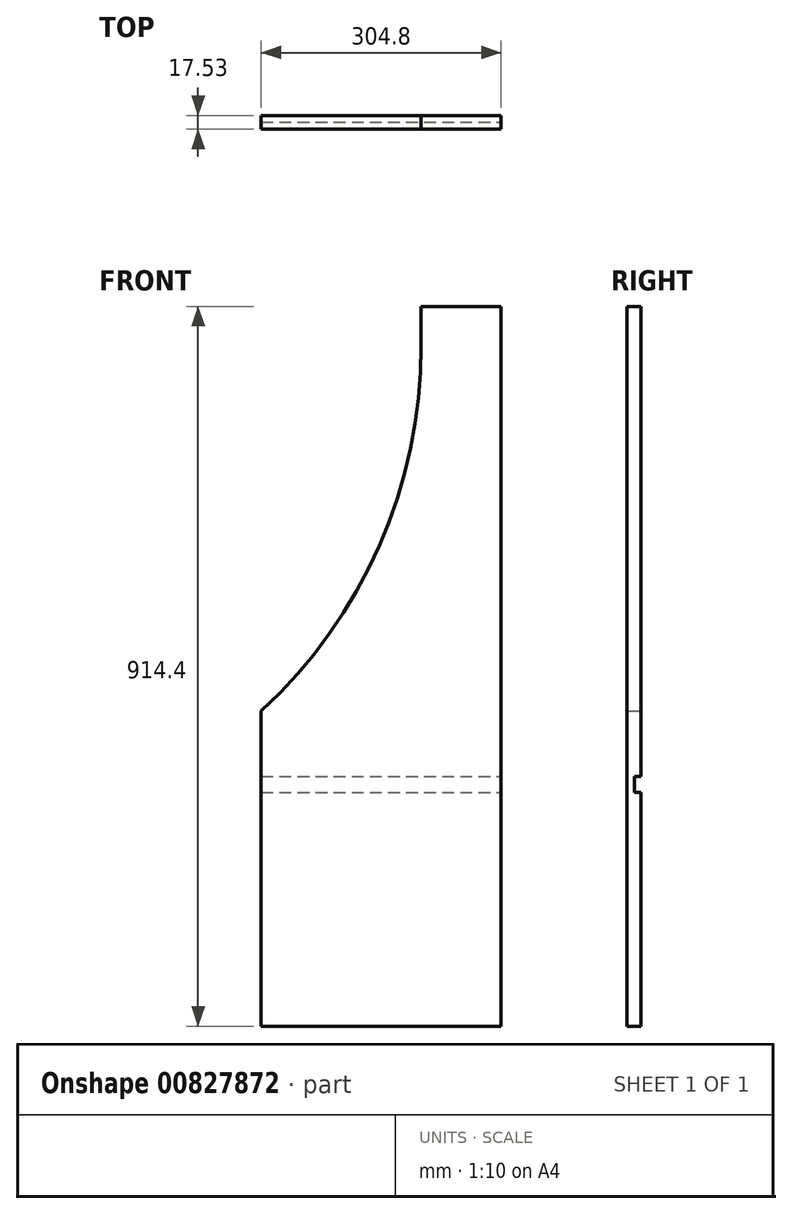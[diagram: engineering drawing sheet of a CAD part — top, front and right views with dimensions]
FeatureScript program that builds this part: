
annotation { "Feature Type Name" : "Feature", "Feature Type Description" : "" }
export const myFeature = defineFeature(function(context is Context, id is Id, definition is map)
    precondition{}
    {
        {
            var Q0;
            Q0=qCreatedBy(makeId("Front.planeOp"),FACE);
            var sketch = newSketch(context, id + "F0", { "sketchPlane" : qUnion([Q0])});
            skLineSegment(sketch, "E0", {"start": v(-178.85, -637.23) * mm, "end": v(125.95, -637.23) * mm});
            skLineSegment(sketch, "E1", {"start": v(125.95, -637.23) * mm, "end": v(125.95, 277.17) * mm});
            skLineSegment(sketch, "E2", {"start": v(125.95, 277.17) * mm, "end": v(24.35, 277.17) * mm});
            skLineSegment(sketch, "E3", {"start": v(24.35, 277.17) * mm, "end": v(24.35, 226.37) * mm});
            skLineSegment(sketch, "E4", {"start": v(-178.85, -637.23) * mm, "end": v(-178.85, -319.73) * mm});
            skArc(sketch, "E5", {"start": v(-178.85, -236.92) * mm, "mid": v(-28.68, -26.58) * mm, "end": v(24.35, 226.37) * mm});
            skLineSegment(sketch, "E6", {"start": v(-178.85, -236.92) * mm, "end": v(-178.85, -319.73) * mm});
            skLineSegment(sketch, "E7.left", {"start": v(-178.85, -258) * mm, "end": v(-178.85, -299.41) * mm});
            skLineSegment(sketch, "E7.right", {"start": v(125.95, -258) * mm, "end": v(125.95, -278.32) * mm});
            skLineSegment(sketch, "E8.left", {"start": v(-178.85, -299.41) * mm, "end": v(-178.85, -319.73) * mm});
            skLineSegment(sketch, "E8.right", {"start": v(125.95, -299.41) * mm, "end": v(125.95, -319.73) * mm});
            skPoint(sketch, "E9", {"position": v(-178.85, -340.05) * mm});
            skLineSegment(sketch, "E10.bottom", {"start": v(-178.85, -319.73) * mm, "end": v(125.95, -319.73) * mm});
            skLineSegment(sketch, "E10.top", {"start": v(-178.85, -340.05) * mm, "end": v(125.95, -340.05) * mm});
            skLineSegment(sketch, "E10.left", {"start": v(-178.85, -319.73) * mm, "end": v(-178.85, -340.05) * mm});
            skLineSegment(sketch, "E10.right", {"start": v(125.95, -319.73) * mm, "end": v(125.95, -340.05) * mm});
            skSolve(sketch);
        }
        {
            var Q0;
            Q0 = qSketchRegion(id + "F0", true);
            extrude(context, id + "F1", {"entities" : qUnion([Q0]), "depth" : 17.53 * mm, "offsetDistance" : 25.4 * mm});
        }
        {
            var Q0;
            Q0=makeQuery(id+"F0.imprint","IMPRINT",FACE,{"disambiguationData":[TD([[makeQuery(id+"F0.imprint","IMPRINT",EDGE,{"derivedFrom":sQuery(id+"F0.wireOp",EDGE,"E10.bottom")}),-1.0]])]});
            extrude(context, id + "F2", {"entities" : qUnion([Q0]), "operationType" : NewBodyOperationType.REMOVE, "surfaceOperationType" : NewSurfaceOperationType.ADD, "depth" : 8.25 * mm, "offsetDistance" : 25.4 * mm});
        }
    });
